# Revit family: QF_HOSHIZAKI_IM-240DPE_251030082052
name_source: partatom
category: Specialty Equipment
units: mm (PartAtom-declared; Revit-internal decimal feet)

## family parameters
Always vertical = Yes
Cut with Voids When Loaded = No
OmniClass Number = 23.40.40.14
OmniClass Title = Food Service Equipment
Part Type = Normal
Room Calculation Point = No
Round Connector Dimension = Use Diameter
Shared = No
Work Plane-Based = No

## types (1)
- M120
    Cost = 7035 $
    Default Elevation = 0 mm  [stored 0 ft]
    Description = CUBE MODEL IS A MODULAR AND STACKABLE ICE MAKER PRODUCING UP TO 210 KG OF CUBE ICE PER 24 HOURS. THIS MODEL IS COMPATIBLE WITH HOSHIZAKI STORAGE BINS
    Manufacturer = HOSHIZAKI
    Model = IM-240DPE
    URL = www.hoshizaki-europe.com

note: [stored X ft] marks values corroborated as IEEE doubles in the binary element streams (Revit-internal decimal feet)

## geometry (parser evidence)
native form markers: Sweep x6
no freeform markers — native parametric forms only
